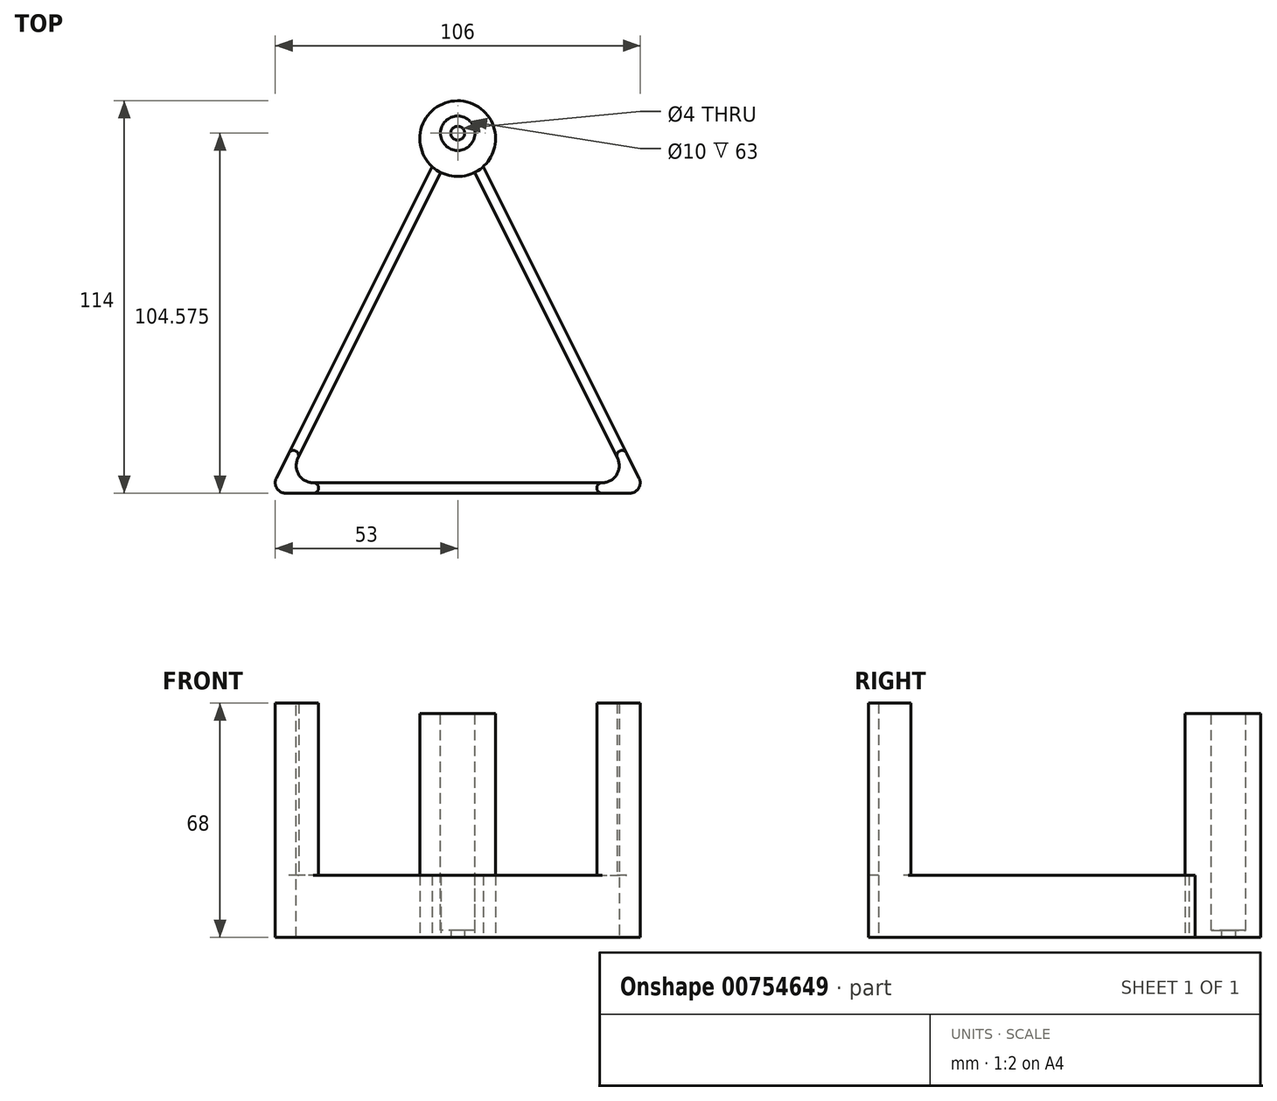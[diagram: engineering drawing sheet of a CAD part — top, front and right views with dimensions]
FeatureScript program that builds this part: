
annotation { "Feature Type Name" : "Feature", "Feature Type Description" : "" }
export const myFeature = defineFeature(function(context is Context, id is Id, definition is map)
    precondition{}
    {
        {
            var Q0;
            Q0=qCreatedBy(makeId("Top.planeOp"),FACE);
            var sketch = newSketch(context, id + "F0", { "sketchPlane" : qUnion([Q0])});
            skLineSegment(sketch, "E0", {"start": v(-50, 0) * mm, "end": v(50, 0) * mm});
            skLineSegment(sketch, "E1", {"start": v(0, 100) * mm, "end": v(50, 0) * mm});
            skLineSegment(sketch, "E2", {"start": v(0, 100) * mm, "end": v(-50, 0) * mm});
            skCircle(sketch, "E3", {"center": v(0, 100) * mm, "radius": 11 * mm});
            skLineSegment(sketch, "E4.0", {"start": v(2.68, 101.34) * mm, "end": v(52.68, 1.34) * mm});
            skLineSegment(sketch, "E5.0", {"start": v(-2.68, 101.34) * mm, "end": v(-52.68, 1.34) * mm});
            skLineSegment(sketch, "E6.0", {"start": v(-50, -3) * mm, "end": v(50, -3) * mm});
            skArc(sketch, "E7", {"start": v(2.68, 101.34) * mm, "mid": v(0, 103) * mm, "end": v(-2.68, 101.34) * mm});
            skArc(sketch, "E8", {"start": v(52.68, 1.34) * mm, "mid": v(52.55, -1.58) * mm, "end": v(50, -3) * mm});
            skArc(sketch, "E9", {"start": v(-50, -3) * mm, "mid": v(-52.55, -1.58) * mm, "end": v(-52.68, 1.34) * mm});
            skCircle(sketch, "E10", {"center": v(0, 101.57) * mm, "radius": 2 * mm});
            skPoint(sketch, "E10.centerSnap0", {"position": v(0, 103) * mm});
            skCircle(sketch, "E11", {"center": v(0, 101.57) * mm, "radius": 5 * mm});
            skSolve(sketch);
        }
        {
            var Q0;
            {var subQ0=sQuery(id+"F0.wireOp",EDGE,"E5.0");var subQ1=sQuery(id+"F0.wireOp",EDGE,"E3");var subQ2=makeQuery(id+"F0.imprint","INTERSECT",VERTEX,{"derivedFrom":[subQ1,subQ0]});Q0=makeQuery(id+"F0.imprint","IMPRINT",FACE,{"disambiguationData":[TD([[makeQuery(id+"F0.imprint","IMPRINT",EDGE,{"disambiguationData":[TD([[subQ2,1.0]])],"derivedFrom":subQ1}),-1.0]])]});}
            var Q1;
            {var subQ5=sQuery(id+"F0.wireOp",EDGE,"E5.0");var subQ7=sQuery(id+"F0.wireOp",EDGE,"E3");var subQ8=makeQuery(id+"F0.imprint","INTERSECT",VERTEX,{"derivedFrom":[subQ7,subQ5]});Q1=makeQuery(id+"F0.imprint","IMPRINT",FACE,{"disambiguationData":[TD([[makeQuery(id+"F0.imprint","IMPRINT",EDGE,{"disambiguationData":[TD([[subQ8,1.0]])],"derivedFrom":subQ7}),1.0]])]});}
            var Q2;
            {var subQ0=sQuery(id+"F0.wireOp",EDGE,"E11");var subQ1=sQuery(id+"F0.wireOp",EDGE,"E1");var subQ2=makeQuery(id+"F0.imprint","INTERSECT",VERTEX,{"derivedFrom":[subQ1,subQ0]});Q2=makeQuery(id+"F0.imprint","IMPRINT",FACE,{"disambiguationData":[TD([[makeQuery(id+"F0.imprint","IMPRINT",EDGE,{"disambiguationData":[TD([[subQ2,-1.0]])],"derivedFrom":subQ1}),-1.0]])]});}
            var Q3;
            {var subQ0=sQuery(id+"F0.wireOp",EDGE,"E11");var subQ1=sQuery(id+"F0.wireOp",EDGE,"E2");var subQ2=makeQuery(id+"F0.imprint","INTERSECT",VERTEX,{"derivedFrom":[subQ1,subQ0]});Q3=makeQuery(id+"F0.imprint","IMPRINT",FACE,{"disambiguationData":[TD([[makeQuery(id+"F0.imprint","IMPRINT",EDGE,{"disambiguationData":[TD([[subQ2,-1.0]])],"derivedFrom":subQ1}),-1.0]])]});}
            var Q4;
            {var subQ0=sQuery(id+"F0.wireOp",EDGE,"E11");var subQ1=sQuery(id+"F0.wireOp",EDGE,"E1");var subQ2=makeQuery(id+"F0.imprint","INTERSECT",VERTEX,{"derivedFrom":[subQ1,subQ0]});Q4=makeQuery(id+"F0.imprint","IMPRINT",FACE,{"disambiguationData":[TD([[makeQuery(id+"F0.imprint","IMPRINT",EDGE,{"disambiguationData":[TD([[subQ2,-1.0]])],"derivedFrom":subQ1}),1.0]])]});}
            var Q5;
            {var subQ0=sQuery(id+"F0.wireOp",EDGE,"E10");var subQ1=sQuery(id+"F0.wireOp",EDGE,"E1");var subQ2=makeQuery(id+"F0.imprint","INTERSECT",VERTEX,{"derivedFrom":[subQ1,subQ0]});Q5=makeQuery(id+"F0.imprint","IMPRINT",FACE,{"disambiguationData":[TD([[makeQuery(id+"F0.imprint","IMPRINT",EDGE,{"disambiguationData":[TD([[subQ2,-1.0]])],"derivedFrom":subQ1}),-1.0]])]});}
            var Q6;
            {var subQ3=sQuery(id+"F0.wireOp",EDGE,"E10");var subQ6=sQuery(id+"F0.wireOp",EDGE,"E2");var subQ9=makeQuery(id+"F0.imprint","INTERSECT",VERTEX,{"derivedFrom":[subQ6,subQ3]});Q6=makeQuery(id+"F0.imprint","IMPRINT",FACE,{"disambiguationData":[TD([[makeQuery(id+"F0.imprint","IMPRINT",EDGE,{"disambiguationData":[TD([[subQ9,-1.0]])],"derivedFrom":subQ6}),-1.0]])]});}
            var Q7;
            {var subQ0=sQuery(id+"F0.wireOp",EDGE,"E7");var subQ5=sQuery(id+"F0.wireOp",EDGE,"E4.0");var subQ6=makeQuery(id+"F0.imprint","INTERSECT",VERTEX,{"derivedFrom":[subQ5,subQ0]});Q7=makeQuery(id+"F0.imprint","IMPRINT",FACE,{"disambiguationData":[TD([[makeQuery(id+"F0.imprint","IMPRINT",EDGE,{"disambiguationData":[TD([[subQ6,-1.0]])],"derivedFrom":subQ5}),1.0]])]});}
            var Q8;
            {var subQ0=sQuery(id+"F0.wireOp",EDGE,"E10");var subQ1=sQuery(id+"F0.wireOp",EDGE,"E1");var subQ2=makeQuery(id+"F0.imprint","INTERSECT",VERTEX,{"derivedFrom":[subQ1,subQ0]});Q8=makeQuery(id+"F0.imprint","IMPRINT",FACE,{"disambiguationData":[TD([[makeQuery(id+"F0.imprint","IMPRINT",EDGE,{"disambiguationData":[TD([[subQ2,-1.0]])],"derivedFrom":subQ1}),1.0]])]});}
            var Q9;
            {var subQ0=sQuery(id+"F0.wireOp",EDGE,"E2");var subQ1=sQuery(id+"F0.wireOp",EDGE,"E1");var subQ2=makeQuery(id+"F0.imprint","INTERSECT",VERTEX,{"derivedFrom":[subQ1,subQ0]});Q9=makeQuery(id+"F0.imprint","IMPRINT",FACE,{"disambiguationData":[TD([[makeQuery(id+"F0.imprint","IMPRINT",EDGE,{"disambiguationData":[TD([[subQ2,-1.0]])],"derivedFrom":subQ1}),1.0]])]});}
            var Q10;
            {var subQ0=sQuery(id+"F0.wireOp",EDGE,"E2");var subQ1=sQuery(id+"F0.wireOp",EDGE,"E1");var subQ2=makeQuery(id+"F0.imprint","INTERSECT",VERTEX,{"derivedFrom":[subQ1,subQ0]});Q10=makeQuery(id+"F0.imprint","IMPRINT",FACE,{"disambiguationData":[TD([[makeQuery(id+"F0.imprint","IMPRINT",EDGE,{"disambiguationData":[TD([[subQ2,-1.0]])],"derivedFrom":subQ1}),-1.0]])]});}
            var Q11;
            {var subQ0=sQuery(id+"F0.wireOp",EDGE,"E10");var subQ1=sQuery(id+"F0.wireOp",EDGE,"E7");var subQ2=makeQuery(id+"F0.imprint","INTERSECT",VERTEX,{"disambiguationData":[OD(0.0)],"derivedFrom":[subQ1,subQ0]});Q11=makeQuery(id+"F0.imprint","IMPRINT",FACE,{"disambiguationData":[TD([[makeQuery(id+"F0.imprint","IMPRINT",EDGE,{"disambiguationData":[TD([[subQ2,-1.0]])],"derivedFrom":subQ1}),-1.0]])]});}
            extrude(context, id + "F1", {"entities" : qUnion([Q0, Q1, Q2, Q3, Q4, Q5, Q6, Q7, Q8, Q9, Q10, Q11]), "depth" : 65 * mm, "offsetDistance" : 25 * mm});
        }
        {
            var Q0;
            {var subQ1=sQuery(id+"F0.wireOp",EDGE,"E0");Q0=makeQuery(id+"F0.imprint","IMPRINT",FACE,{"disambiguationData":[TD([[makeQuery(id+"F0.imprint","IMPRINT",EDGE,{"derivedFrom":subQ1}),-1.0]])]});}
            extrude(context, id + "F2", {"entities" : qUnion([Q0]), "operationType" : NewBodyOperationType.ADD, "depth" : 18 * mm, "offsetDistance" : 25 * mm});
        }
        {
            var Q0;
            {var subQ0=sQuery(id+"F0.wireOp",EDGE,"E2");var subQ1=sQuery(id+"F0.wireOp",EDGE,"E1");var subQ2=makeQuery(id+"F0.imprint","INTERSECT",VERTEX,{"derivedFrom":[subQ1,subQ0]});Q0=makeQuery(id+"F0.imprint","IMPRINT",FACE,{"disambiguationData":[TD([[makeQuery(id+"F0.imprint","IMPRINT",EDGE,{"disambiguationData":[TD([[subQ2,-1.0]])],"derivedFrom":subQ1}),1.0]])]});}
            var Q1;
            {var subQ0=sQuery(id+"F0.wireOp",EDGE,"E10");var subQ1=sQuery(id+"F0.wireOp",EDGE,"E7");var subQ2=makeQuery(id+"F0.imprint","INTERSECT",VERTEX,{"disambiguationData":[OD(0.0)],"derivedFrom":[subQ1,subQ0]});Q1=makeQuery(id+"F0.imprint","IMPRINT",FACE,{"disambiguationData":[TD([[makeQuery(id+"F0.imprint","IMPRINT",EDGE,{"disambiguationData":[TD([[subQ2,-1.0]])],"derivedFrom":subQ1}),-1.0]])]});}
            var Q2;
            {var subQ0=sQuery(id+"F0.wireOp",EDGE,"E2");var subQ1=sQuery(id+"F0.wireOp",EDGE,"E1");var subQ2=makeQuery(id+"F0.imprint","INTERSECT",VERTEX,{"derivedFrom":[subQ1,subQ0]});Q2=makeQuery(id+"F0.imprint","IMPRINT",FACE,{"disambiguationData":[TD([[makeQuery(id+"F0.imprint","IMPRINT",EDGE,{"disambiguationData":[TD([[subQ2,-1.0]])],"derivedFrom":subQ1}),-1.0]])]});}
            extrude(context, id + "F3", {"entities" : qUnion([Q0, Q1, Q2]), "operationType" : NewBodyOperationType.REMOVE, "depth" : 65 * mm, "offsetDistance" : 25 * mm});
        }
        {
            var Q0;
            Q0=makeQuery(id+"F2.opExtrude","SWEPT_EDGE",EDGE,{"disambiguationData":[OSD([sQuery(id+"F0.wireOp",EDGE,"E0"),sQuery(id+"F0.wireOp",EDGE,"E1")])]});
            fillet(context, id + "F4", {"entities" : qUnion([Q0]), "radius" : 5 * mm, "tangentPropagation" : true, "allowEdgeOverflow" : false});
        }
        {
            var Q0;
            Q0=makeQuery(id+"F2.opExtrude","SWEPT_EDGE",EDGE,{"disambiguationData":[OSD([sQuery(id+"F0.wireOp",EDGE,"E2"),sQuery(id+"F0.wireOp",EDGE,"fa103425-687d-4ccd-9b05-93ddf02f588a.0")])]});
            var Q1;
            Q1=makeQuery(id+"F2.opExtrude","SWEPT_EDGE",EDGE,{"disambiguationData":[OSD([sQuery(id+"F0.wireOp",EDGE,"E1"),sQuery(id+"F0.wireOp",EDGE,"fa103425-687d-4ccd-9b05-93ddf02f588a.0")])]});
            var Q2;
            Q2=makeQuery(id+"F2.opExtrude","SWEPT_EDGE",EDGE,{"disambiguationData":[OSD([sQuery(id+"F0.wireOp",EDGE,"E0"),sQuery(id+"F0.wireOp",EDGE,"E2")])]});
            var Q3;
            Q3=makeQuery(id+"F2.opExtrude","SWEPT_EDGE",EDGE,{"disambiguationData":[OSD([sQuery(id+"F0.wireOp",EDGE,"E5.0"),sQuery(id+"F0.wireOp",EDGE,"fa103425-687d-4ccd-9b05-93ddf02f588a.0")])]});
            var Q4;
            Q4=makeQuery(id+"F2.opExtrude","SWEPT_EDGE",EDGE,{"disambiguationData":[OSD([sQuery(id+"F0.wireOp",EDGE,"E4.0"),sQuery(id+"F0.wireOp",EDGE,"fa103425-687d-4ccd-9b05-93ddf02f588a.0")])]});
            fillet(context, id + "F5", {"entities" : qUnion([Q0, Q1, Q2, Q3, Q4]), "radius" : 5 * mm, "tangentPropagation" : true, "allowEdgeOverflow" : false});
        }
        {
            var Q0;
            Q0=makeQuery(id+"F2.opExtrude","CAP_FACE",FACE,{"disambiguationData":[OSD([sQuery(id+"F0.wireOp",EDGE,"E0"),sQuery(id+"F0.wireOp",EDGE,"E1"),sQuery(id+"F0.wireOp",EDGE,"E2"),sQuery(id+"F0.wireOp",EDGE,"E4.0"),sQuery(id+"F0.wireOp",EDGE,"E5.0"),sQuery(id+"F0.wireOp",EDGE,"E6.0"),sQuery(id+"F0.wireOp",EDGE,"E8"),sQuery(id+"F0.wireOp",EDGE,"E9"),sQuery(id+"F0.wireOp",EDGE,"fa103425-687d-4ccd-9b05-93ddf02f588a.0")])],"isStart":false});
            var sketch = newSketch(context, id + "F6", { "sketchPlane" : qUnion([Q0])});
            skArc(sketch, "E12", {"start": v(-41.9, -3) * mm, "mid": v(-40.4, -1.5) * mm, "end": v(-41.9, 0) * mm});
            skArc(sketch, "E13", {"start": v(-46.38, 7.24) * mm, "mid": v(-47.05, 9.25) * mm, "end": v(-49.07, 8.58) * mm});
            skArc(sketch, "E14", {"start": v(41.9, 0) * mm, "mid": v(40.4, -1.5) * mm, "end": v(41.9, -3) * mm});
            skArc(sketch, "E15", {"start": v(49.07, 8.58) * mm, "mid": v(47.05, 9.25) * mm, "end": v(46.38, 7.24) * mm});
            skSolve(sketch);
        }
        {
            var Q0;
            {var subQ7=sQuery(id+"F6.wireOp",EDGE,"E14");Q0=makeQuery(id+"F6.imprint","IMPRINT",FACE,{"disambiguationData":[TD([[makeQuery(id+"F6.imprint","IMPRINT",EDGE,{"derivedFrom":subQ7}),1.0]])]});}
            var Q1;
            {var subQ7=sQuery(id+"F6.wireOp",EDGE,"E12");Q1=makeQuery(id+"F6.imprint","IMPRINT",FACE,{"disambiguationData":[TD([[makeQuery(id+"F6.imprint","IMPRINT",EDGE,{"derivedFrom":subQ7}),1.0]])]});}
            extrude(context, id + "F7", {"entities" : qUnion([Q0, Q1]), "operationType" : NewBodyOperationType.ADD, "depth" : 50 * mm, "offsetDistance" : 25 * mm});
        }
        {
            var Q0;
            Q0=makeQuery(id+"F1.opExtrude","CAP_FACE",FACE,{"disambiguationData":[OSD([sQuery(id+"F0.wireOp",EDGE,"E3")])],"isStart":false});
            var sketch = newSketch(context, id + "F8", { "sketchPlane" : qUnion([Q0])});
            skCircle(sketch, "E16", {"center": v(0, 101.57) * mm, "radius": 5 * mm});
            skSolve(sketch);
        }
        {
            var Q0;
            Q0=makeQuery(id+"F8.imprint","IMPRINT",FACE,{"disambiguationData":[TD([[makeQuery(id+"F8.imprint","IMPRINT",EDGE,{"derivedFrom":sQuery(id+"F8.wireOp",EDGE,"E16")}),1.0]])]});
            extrude(context, id + "F9", {"entities" : qUnion([Q0]), "operationType" : NewBodyOperationType.REMOVE, "oppositeDirection" : true, "depth" : 63 * mm, "offsetDistance" : 25 * mm});
        }
    });
